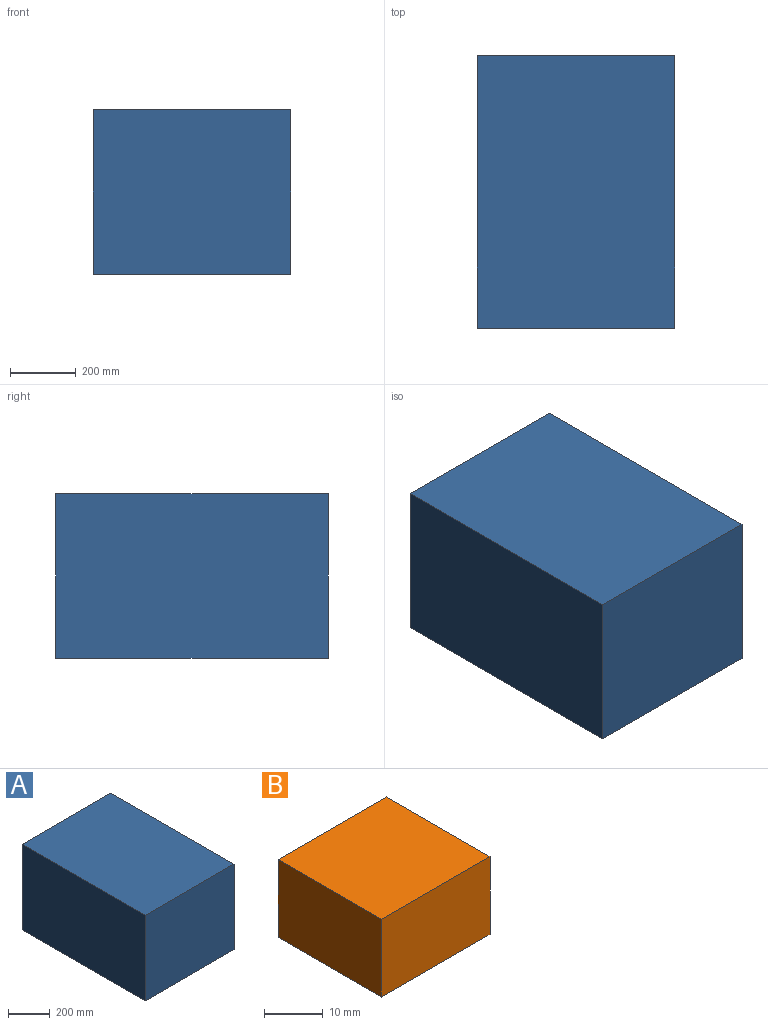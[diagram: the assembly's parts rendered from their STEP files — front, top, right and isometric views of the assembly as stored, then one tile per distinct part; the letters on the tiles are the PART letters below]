
ASSEMBLY  parts=2 mates=1
PART A: 6 faces, bbox 600x830x500 mm
  f0: plane 830x600mm, normal (0,0,-1), area 498000mm2, adj f1,f3,f4,f5
  f1: plane 830x500mm, normal (1,0,0), area 415000mm2, adj f0,f2,f4,f5
  f2: plane 830x600mm, normal (0,0,1), area 498000mm2, adj f1,f3,f4,f5
  f3: plane 830x500mm, normal (-1,0,0), area 415000mm2, adj f0,f2,f4,f5
  f4: plane 600x500mm, normal (0,-1,0), area 300000mm2, adj f0,f1,f2,f3
  f5: plane 600x500mm, normal (0,1,0), area 300000mm2, adj f0,f1,f2,f3
PART B: 6 faces, bbox 26.2x25x16.3 mm
  f0: plane 26.22x25mm, normal (0,0,-1), area 655.4mm2, adj f1,f3,f4,f5
  f1: plane 25x16.26mm, normal (1,0,0), area 406.5mm2, adj f0,f2,f4,f5
  f2: plane 26.22x25mm, normal (0,0,1), area 655.4mm2, adj f1,f3,f4,f5
  f3: plane 25x16.26mm, normal (-1,0,0), area 406.5mm2, adj f0,f2,f4,f5
  f4: plane 26.22x16.26mm, normal (0,-1,0), area 426.2mm2, adj f0,f1,f2,f3
  f5: plane 26.22x16.26mm, normal (0,1,0), area 426.2mm2, adj f0,f1,f2,f3
PLACE A t=(-13.47,-6.84,1.41)mm fixed
PLACE B t=(-13.47,5.66,73.55)mm
MATE slider B.f0 <-> A.f2  axis (0,0,-1) through (-13.47,-6.84,65.42)mm
